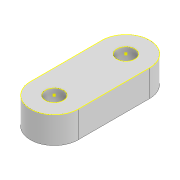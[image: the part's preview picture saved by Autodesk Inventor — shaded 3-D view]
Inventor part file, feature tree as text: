
AUTODESK INVENTOR PART (.ipt)
format: ipt  version: 2022 (Build 260153000, 153)  size: 100,352 bytes
history: native  units: mm
features: sketch x2, extrude x1, projected_geometry x1
ambient origin geometry x8: Origin, YZ Plane, XZ Plane, XY Plane, X Axis, Y Axis, Z Axis, Center Point
bodies: Solid1 (feature_tree)
feature tree (4):
  extrude  "Extrusion1"  Depth=8.0mm
  sketch  "Sketch2"  dims[d3=3.0mm d4=6.0mm d5=4.5mm d6=0.0mm]
  sketch  "Sketch1"  dims[d1=8.0mm d2=3.0mm]
  projected_geometry  "Projected Loop1"
